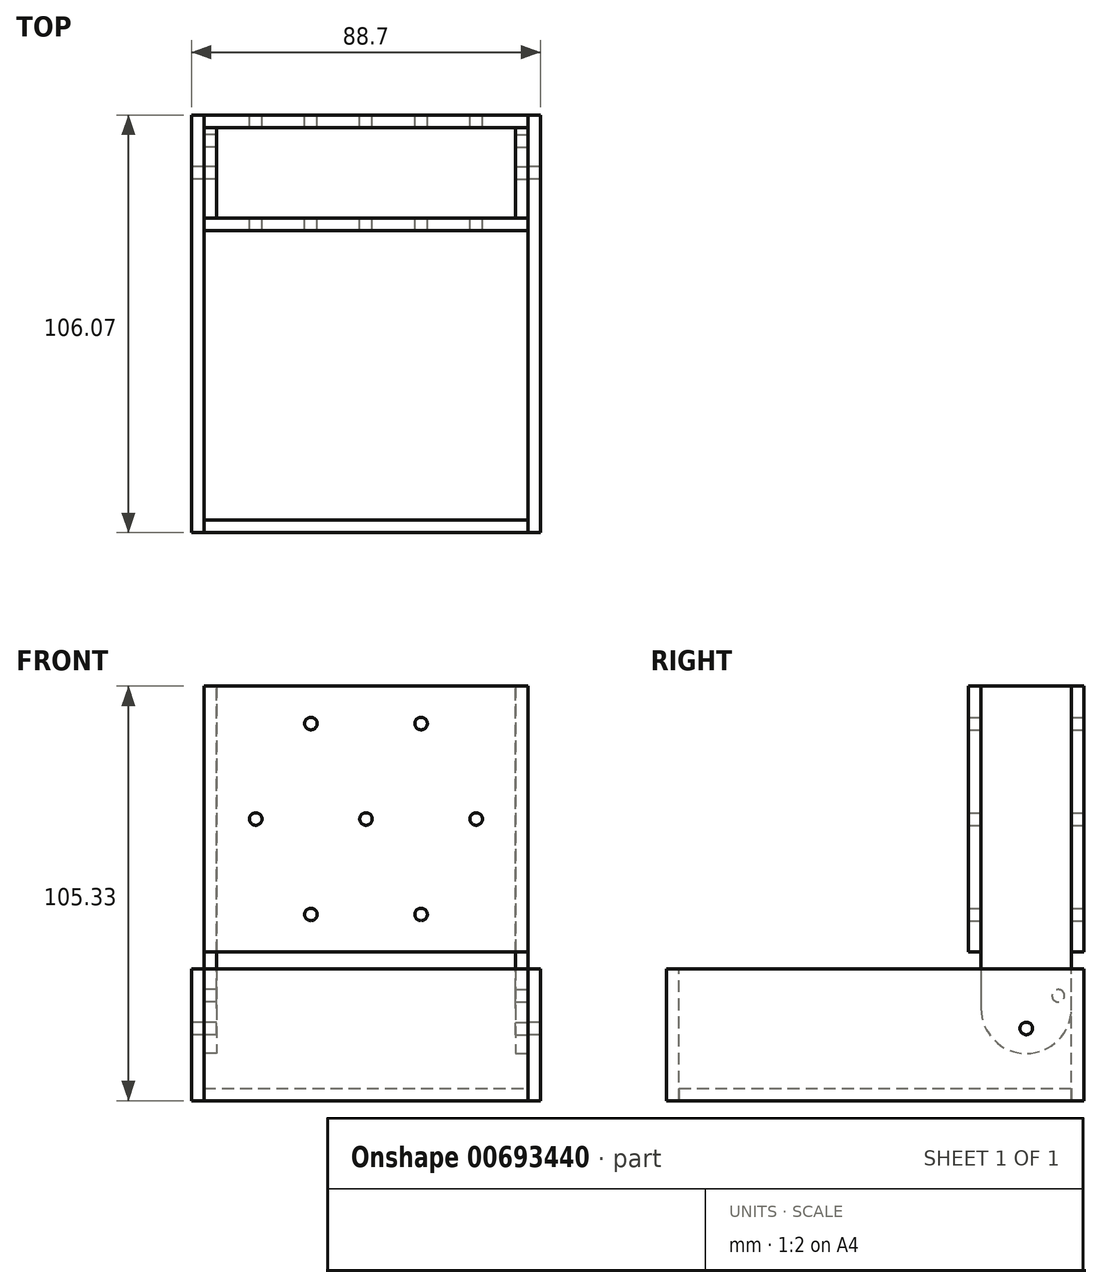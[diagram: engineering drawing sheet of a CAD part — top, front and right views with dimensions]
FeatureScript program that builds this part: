
annotation { "Feature Type Name" : "Feature", "Feature Type Description" : "" }
export const myFeature = defineFeature(function(context is Context, id is Id, definition is map)
    precondition{}
    {
        {
            var Q0;
            Q0=qCreatedBy(makeId("Front.planeOp"),FACE);
            var sketch = newSketch(context, id + "F0", { "sketchPlane" : qUnion([Q0])});
            skCircle(sketch, "E0", {"center": v(0, 0) * mm, "radius": 1.59 * mm});
            skCircle(sketch, "E1", {"center": v(28, 0) * mm, "radius": 1.59 * mm});
            skCircle(sketch, "E2.1.0", {"center": v(14, 24.25) * mm, "radius": 1.59 * mm});
            skCircle(sketch, "E2.2.0", {"center": v(-14, 24.25) * mm, "radius": 1.59 * mm});
            skCircle(sketch, "E2.3.0", {"center": v(-28, 0) * mm, "radius": 1.59 * mm});
            skCircle(sketch, "E2.4.0", {"center": v(-14, -24.25) * mm, "radius": 1.59 * mm});
            skCircle(sketch, "E2.5.0", {"center": v(14, -24.25) * mm, "radius": 1.59 * mm});
            skLineSegment(sketch, "E3.bottom", {"start": v(41.17, -33.77) * mm, "end": v(-41.17, -33.77) * mm});
            skLineSegment(sketch, "E3.top", {"start": v(41.17, 33.77) * mm, "end": v(-41.17, 33.77) * mm});
            skLineSegment(sketch, "E3.left", {"start": v(41.17, -33.77) * mm, "end": v(41.17, 33.77) * mm});
            skLineSegment(sketch, "E3.right", {"start": v(-41.17, -33.77) * mm, "end": v(-41.17, 33.77) * mm});
            skLineSegment(sketch, "E4", {"start": v(-38, 33.77) * mm, "end": v(-38, -33.77) * mm});
            skLineSegment(sketch, "E5", {"start": v(38, 33.77) * mm, "end": v(38, -33.77) * mm});
            skLineSegment(sketch, "E6", {"start": v(-41.17, -33.77) * mm, "end": v(-41.17, -57.77) * mm});
            skLineSegment(sketch, "E7", {"start": v(-41.17, -57.77) * mm, "end": v(41.17, -57.77) * mm});
            skLineSegment(sketch, "E8", {"start": v(41.17, -57.77) * mm, "end": v(41.17, -33.77) * mm});
            skLineSegment(sketch, "E9", {"start": v(41.17, -57.77) * mm, "end": v(41.17, -60.95) * mm});
            skLineSegment(sketch, "E10", {"start": v(41.17, -60.95) * mm, "end": v(41.17, -64.12) * mm});
            skLineSegment(sketch, "E11", {"start": v(41.17, -64.12) * mm, "end": v(-41.17, -64.12) * mm});
            skLineSegment(sketch, "E12", {"start": v(-41.17, -64.12) * mm, "end": v(-41.17, -60.95) * mm});
            skLineSegment(sketch, "E13", {"start": v(-41.17, -60.95) * mm, "end": v(-41.17, -57.77) * mm});
            skLineSegment(sketch, "E14", {"start": v(-41.17, -60.95) * mm, "end": v(41.17, -60.95) * mm});
            skSolve(sketch);
        }
        {
            var Q0;
            {var subQ0=sQuery(id+"F0.wireOp",EDGE,"E3.left");Q0=makeQuery(id+"F0.imprint","IMPRINT",FACE,{"disambiguationData":[TD([[makeQuery(id+"F0.imprint","IMPRINT",EDGE,{"derivedFrom":subQ0}),1.0]])]});}
            var Q1;
            Q1=makeQuery(id+"F0.imprint","IMPRINT",FACE,{"disambiguationData":[TD([[makeQuery(id+"F0.imprint","IMPRINT",EDGE,{"derivedFrom":sQuery(id+"F0.wireOp",EDGE,"E0")}),-1.0]])]});
            var Q2;
            {var subQ0=sQuery(id+"F0.wireOp",EDGE,"E3.right");Q2=makeQuery(id+"F0.imprint","IMPRINT",FACE,{"disambiguationData":[TD([[makeQuery(id+"F0.imprint","IMPRINT",EDGE,{"derivedFrom":subQ0}),-1.0]])]});}
            extrude(context, id + "F1", {"entities" : qUnion([Q0, Q1, Q2]), "depth" : 3.17 * mm, "offsetDistance" : 25 * mm});
        }
        {
            var Q0;
            Q0=makeQuery(id+"F1.opExtrude","SWEPT_FACE",FACE,{"disambiguationData":[OSD([sQuery(id+"F0.wireOp",EDGE,"E3.left")])]});
            var sketch = newSketch(context, id + "F2", { "sketchPlane" : qUnion([Q0])});
            skLineSegment(sketch, "E15.bottom", {"start": v(-3.17, 33.77) * mm, "end": v(-26.18, 33.77) * mm});
            skLineSegment(sketch, "E15.top", {"start": v(-3.17, -48.06) * mm, "end": v(-26.18, -48.06) * mm, "construction": true});
            skLineSegment(sketch, "E15.left", {"start": v(-3.18, 33.77) * mm, "end": v(-3.17, -48.06) * mm});
            skLineSegment(sketch, "E15.right", {"start": v(-26.18, 33.77) * mm, "end": v(-26.17, -48.06) * mm});
            skArc(sketch, "E16", {"start": v(-26.17, -48.06) * mm, "mid": v(-14.68, -59.56) * mm, "end": v(-3.18, -48.06) * mm});
            skCircle(sketch, "E17", {"center": v(-14.68, -53.21) * mm, "radius": 1.59 * mm});
            skLineSegment(sketch, "E18", {"start": v(-3.18, -33.77) * mm, "end": v(-13.87, -51.85) * mm, "construction": true});
            skLineSegment(sketch, "E19", {"start": v(-3.18, -33.77) * mm, "end": v(-26.17, -33.77) * mm, "construction": true});
            skCircle(sketch, "E20", {"center": v(-6.53, -44.91) * mm, "radius": 1.59 * mm});
            skLineSegment(sketch, "E21", {"start": v(-14.68, -53.21) * mm, "end": v(-6.53, -44.91) * mm, "construction": true});
            skLineSegment(sketch, "E22", {"start": v(-3.17, -33.77) * mm, "end": v(-6.53, -44.91) * mm, "construction": true});
            skCircle(sketch, "E23", {"center": v(-26.17, -33.77) * mm, "radius": 21 * mm, "construction": true});
            skSolve(sketch);
        }
        {
            var Q0;
            Q0 = qSketchRegion(id + "F2", true);
            extrude(context, id + "F3", {"entities" : qUnion([Q0]), "oppositeDirection" : true, "depth" : 3.17 * mm, "offsetDistance" : 25 * mm});
        }
        {
            var Q0;
            Q0=makeQuery(id+"F3.opExtrude","SWEPT_BODY",BODY,{"disambiguationData":[OSD([sQuery(id+"F2.wireOp",EDGE,"E15.bottom"),sQuery(id+"F2.wireOp",EDGE,"E15.left"),sQuery(id+"F2.wireOp",EDGE,"E15.right"),sQuery(id+"F2.wireOp",EDGE,"E16"),sQuery(id+"F2.wireOp",EDGE,"E17"),sQuery(id+"F2.wireOp",EDGE,"E20")])]});
            var Q1;
            Q1=qCreatedBy(makeId("Right.planeOp"),FACE);
            mirror(context, id + "F4", {"entities" : qUnion([Q0]), "mirrorPlane" : qUnion([Q1])});
        }
        {
            var Q0;
            Q0=makeQuery(id+"F1.opExtrude","SWEPT_BODY",BODY,{"disambiguationData":[OSD([sQuery(id+"F0.wireOp",EDGE,"E0"),sQuery(id+"F0.wireOp",EDGE,"E1"),sQuery(id+"F0.wireOp",EDGE,"E2.1.0"),sQuery(id+"F0.wireOp",EDGE,"E2.2.0"),sQuery(id+"F0.wireOp",EDGE,"E2.3.0"),sQuery(id+"F0.wireOp",EDGE,"E2.4.0"),sQuery(id+"F0.wireOp",EDGE,"E2.5.0"),sQuery(id+"F0.wireOp",EDGE,"E3.bottom"),sQuery(id+"F0.wireOp",EDGE,"E3.top"),sQuery(id+"F0.wireOp",EDGE,"E3.left"),sQuery(id+"F0.wireOp",EDGE,"E3.right")])]});
            transform(context, id + "F5", {"entities" : qUnion([Q0]), "transformType" : TransformType.TRANSLATION_3D, "dx" : 0 * mm, "dy" : -(23 + 3.17) * mm, "dz" : 0 * mm, "makeCopy" : true});
        }
        {
            var Q0;
            Q0=makeQuery(id+"F3.opExtrude","CAP_FACE",FACE,{"disambiguationData":[OSD([sQuery(id+"F2.wireOp",EDGE,"E15.bottom"),sQuery(id+"F2.wireOp",EDGE,"E15.left"),sQuery(id+"F2.wireOp",EDGE,"E15.right"),sQuery(id+"F2.wireOp",EDGE,"E16"),sQuery(id+"F2.wireOp",EDGE,"E17"),sQuery(id+"F2.wireOp",EDGE,"E20")])],"isStart":true});
            var sketch = newSketch(context, id + "F6", { "sketchPlane" : qUnion([Q0])});
            skLineSegment(sketch, "E24.bottom", {"start": v(-106.07, -38.04) * mm, "end": v(0, -38.04) * mm});
            skLineSegment(sketch, "E24.top", {"start": v(-106.07, -71.56) * mm, "end": v(0, -71.56) * mm});
            skLineSegment(sketch, "E24.left", {"start": v(-106.07, -38.04) * mm, "end": v(-106.07, -71.56) * mm});
            skLineSegment(sketch, "E24.right", {"start": v(0, -38.04) * mm, "end": v(0, -71.56) * mm});
            skLineSegment(sketch, "E25", {"start": v(-106.07, -68.39) * mm, "end": v(0, -68.39) * mm, "construction": true});
            skCircle(sketch, "E26", {"center": v(-14.68, -53.21) * mm, "radius": 1.59 * mm});
            skLineSegment(sketch, "E27", {"start": v(-14.67, -53.21) * mm, "end": v(-14.67, 35) * mm, "construction": true});
            skLineSegment(sketch, "E28", {"start": v(-14.68, -53.21) * mm, "end": v(-102.9, -53.21) * mm, "construction": true});
            skLineSegment(sketch, "E29", {"start": v(-29.35, 33.77) * mm, "end": v(-14.68, -53.21) * mm, "construction": true});
            skLineSegment(sketch, "E30", {"start": v(0, 0) * mm, "end": v(-29.35, 0) * mm, "construction": true});
            skLineSegment(sketch, "E31", {"start": v(-53.03, -38.04) * mm, "end": v(-53.03, -67.39) * mm, "construction": true});
            skLineSegment(sketch, "E32", {"start": v(-102.9, -53.21) * mm, "end": v(-106.07, -53.21) * mm, "construction": true});
            skLineSegment(sketch, "E33", {"start": v(-53.03, -71.56) * mm, "end": v(-53.03, -68.39) * mm, "construction": true});
            skLineSegment(sketch, "E34", {"start": v(-106.07, -38.04) * mm, "end": v(-102.9, -53.21) * mm, "construction": true});
            skLineSegment(sketch, "E35", {"start": v(-102.9, -53.21) * mm, "end": v(-106.07, -68.39) * mm, "construction": true});
            skLineSegment(sketch, "E36", {"start": v(-3.18, -48.06) * mm, "end": v(0, -48.06) * mm, "construction": true});
            skSolve(sketch);
        }
        {
            var Q0;
            Q0 = qSketchRegion(id + "F6", true);
            extrude(context, id + "F7", {"entities" : qUnion([Q0]), "depth" : 3.17 * mm, "offsetDistance" : 25 * mm});
        }
        {
            var Q0;
            Q0=makeQuery(id+"F7.opExtrude","SWEPT_FACE",FACE,{"disambiguationData":[OSD([sQuery(id+"F6.wireOp",EDGE,"E24.right")])]});
            var sketch = newSketch(context, id + "F8", { "sketchPlane" : qUnion([Q0])});
            skLineSegment(sketch, "E37.bottom", {"start": v(-41.17, -71.56) * mm, "end": v(41.17, -71.56) * mm});
            skLineSegment(sketch, "E37.top", {"start": v(-41.18, -38.04) * mm, "end": v(41.17, -38.04) * mm});
            skLineSegment(sketch, "E37.left", {"start": v(-41.18, -71.56) * mm, "end": v(-41.18, -38.04) * mm});
            skLineSegment(sketch, "E37.right", {"start": v(41.17, -71.56) * mm, "end": v(41.17, -38.04) * mm});
            skSolve(sketch);
        }
        {
            var Q0;
            Q0 = qSketchRegion(id + "F8", true);
            var Q1;
            Q1=makeQuery(id+"F3.opExtrude","SWEPT_FACE",FACE,{"disambiguationData":[OSD([sQuery(id+"F2.wireOp",EDGE,"E15.left")])]});
            var Q2;
            Q2=makeQuery(id+"F7.opExtrude","CAP_VERTEX",VERTEX,{"disambiguationData":[OSD([sQuery(id+"F6.wireOp",EDGE,"E24.top"),sQuery(id+"F6.wireOp",EDGE,"E24.right")])],"isStart":true});
            extrude(context, id + "F9", {"entities" : qUnion([Q0]), "endBound" : BoundingType.UP_TO_SURFACE, "oppositeDirection" : true, "depth" : 3.17 * mm, "endBoundEntityFace" : qUnion([Q1]), "endBoundEntityVertex" : qUnion([Q2]), "offsetDistance" : 25 * mm});
        }
        {
            var Q0;
            Q0=makeQuery(id+"F7.opExtrude","SWEPT_BODY",BODY,{"disambiguationData":[OSD([sQuery(id+"F6.wireOp",EDGE,"E24.bottom"),sQuery(id+"F6.wireOp",EDGE,"E24.top"),sQuery(id+"F6.wireOp",EDGE,"E24.left"),sQuery(id+"F6.wireOp",EDGE,"E24.right"),sQuery(id+"F6.wireOp",EDGE,"E26")])]});
            transform(context, id + "F10", {"entities" : qUnion([Q0]), "transformType" : TransformType.TRANSLATION_3D, "dx" : -(82.35 + 3.17) * mm, "dy" : 0 * mm, "dz" : 0 * mm, "makeCopy" : true});
        }
        {
            var Q0;
            Q0=makeQuery(id+"F9.opExtrude","SWEPT_BODY",BODY,{"disambiguationData":[OSD([sQuery(id+"F8.wireOp",EDGE,"E37.bottom"),sQuery(id+"F8.wireOp",EDGE,"E37.top"),sQuery(id+"F8.wireOp",EDGE,"E37.left"),sQuery(id+"F8.wireOp",EDGE,"E37.right")])]});
            transform(context, id + "F11", {"entities" : qUnion([Q0]), "transformType" : TransformType.TRANSLATION_3D, "dx" : 0 * mm, "dy" : -(106.07 - 3.17) * mm, "dz" : 0 * mm, "makeCopy" : true});
        }
        {
            var Q0;
            Q0=makeQuery(id+"F10.opPattern","COPY",FACE,{"derivedFrom":makeQuery(id+"F7.opExtrude","SWEPT_FACE",FACE,{"disambiguationData":[OSD([sQuery(id+"F6.wireOp",EDGE,"E24.top")])]}),"instanceName":"1"});
            var sketch = newSketch(context, id + "F12", { "sketchPlane" : qUnion([Q0])});
            skLineSegment(sketch, "E38.bottom", {"start": v(-41.18, 102.9) * mm, "end": v(41.17, 102.9) * mm});
            skLineSegment(sketch, "E38.top", {"start": v(-41.18, 3.17) * mm, "end": v(41.17, 3.17) * mm});
            skLineSegment(sketch, "E38.left", {"start": v(-41.18, 102.9) * mm, "end": v(-41.18, 3.17) * mm});
            skLineSegment(sketch, "E38.right", {"start": v(41.17, 102.9) * mm, "end": v(41.17, 3.17) * mm});
            skSolve(sketch);
        }
        {
            var Q0;
            Q0 = qSketchRegion(id + "F12", true);
            extrude(context, id + "F13", {"entities" : qUnion([Q0]), "oppositeDirection" : true, "depth" : 3.17 * mm, "offsetDistance" : 25 * mm});
        }
    });
